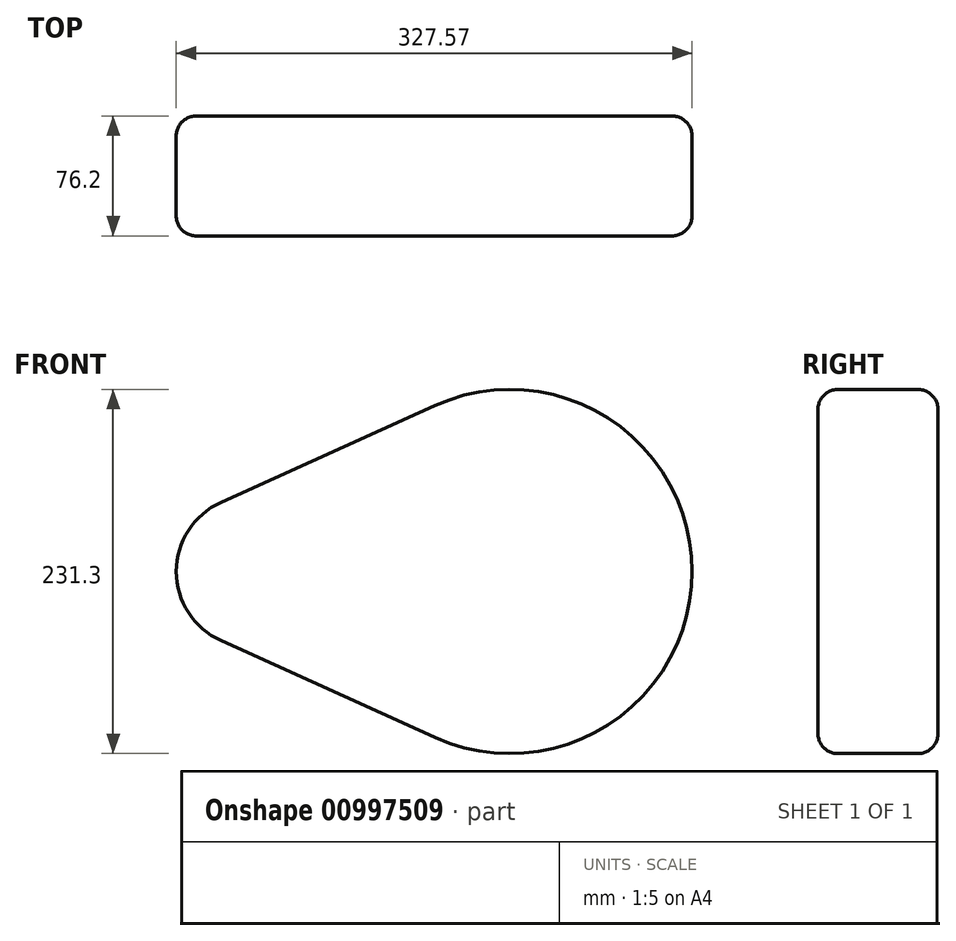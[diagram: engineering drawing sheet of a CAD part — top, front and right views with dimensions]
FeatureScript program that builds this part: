
annotation { "Feature Type Name" : "Feature", "Feature Type Description" : "" }
export const myFeature = defineFeature(function(context is Context, id is Id, definition is map)
    precondition{}
    {
        {
            var Q0;
            Q0=qCreatedBy(makeId("Front.planeOp"),FACE);
            var sketch = newSketch(context, id + "F0", { "sketchPlane" : qUnion([Q0])});
            skCircle(sketch, "E0", {"center": v(-64.8, 0) * mm, "radius": 48.13 * mm});
            skCircle(sketch, "E1", {"center": v(98.99, 0) * mm, "radius": 115.65 * mm});
            skLineSegment(sketch, "E2", {"start": v(-84.64, 43.85) * mm, "end": v(51.31, 105.37) * mm});
            skLineSegment(sketch, "E3", {"start": v(51.31, 105.37) * mm, "end": v(51.31, 105.37) * mm});
            skLineSegment(sketch, "E4", {"start": v(-84.64, -43.85) * mm, "end": v(51.31, -105.37) * mm});
            skSolve(sketch);
        }
        {
            var Q0;
            Q0 = qSketchRegion(id + "F0", true);
            extrude(context, id + "F1", {"entities" : qUnion([Q0]), "depth" : 25.4 * mm, "offsetDistance" : 25.4 * mm});
        }
        {
            var Q0;
            Q0=qCreatedBy(makeId("Front.planeOp"),FACE);
            var sketch = newSketch(context, id + "F2", { "sketchPlane" : qUnion([Q0])});
            skCircle(sketch, "E5", {"center": v(105.69, 0) * mm, "radius": 57.3 * mm});
            skSolve(sketch);
        }
        {
            var Q0;
            Q0=makeQuery(id+"F2.imprint","IMPRINT",FACE,{"disambiguationData":[TD([[makeQuery(id+"F2.imprint","IMPRINT",EDGE,{"derivedFrom":sQuery(id+"F2.wireOp",EDGE,"E5")}),1.0]])]});
            extrude(context, id + "F3", {"entities" : qUnion([Q0]), "operationType" : NewBodyOperationType.REMOVE, "oppositeDirection" : true, "depth" : 25.4 * mm, "offsetDistance" : 25.4 * mm});
        }
        {
            var Q0;
            Q0=makeQuery(id+"F1.opExtrude","CAP_FACE",FACE,{"disambiguationData":[OSD([sQuery(id+"F0.wireOp",EDGE,"E0"),sQuery(id+"F0.wireOp",EDGE,"E1"),sQuery(id+"F0.wireOp",EDGE,"E2"),sQuery(id+"F0.wireOp",EDGE,"E4")])],"isStart":true});
            extrude(context, id + "F4", {"entities" : qUnion([Q0]), "operationType" : NewBodyOperationType.ADD, "depth" : 50.8 * mm, "offsetDistance" : 25.4 * mm});
        }
        {
            var Q0;
            Q0=makeQuery(id+"F4.opExtrude","CAP_EDGE",EDGE,{"disambiguationData":[OSD([sQuery(id+"F0.wireOp",EDGE,"E2")])],"isStart":false});
            fillet(context, id + "F5", {"entities" : qUnion([Q0]), "radius" : 12.7 * mm, "tangentPropagation" : true, "allowEdgeOverflow" : false});
        }
        {
            var Q0;
            Q0=makeQuery(id+"F1.opExtrude","CAP_EDGE",EDGE,{"disambiguationData":[OSD([sQuery(id+"F0.wireOp",EDGE,"E2")])],"isStart":false});
            fillet(context, id + "F6", {"entities" : qUnion([Q0]), "radius" : 12.7 * mm, "tangentPropagation" : true, "allowEdgeOverflow" : false});
        }
    });
